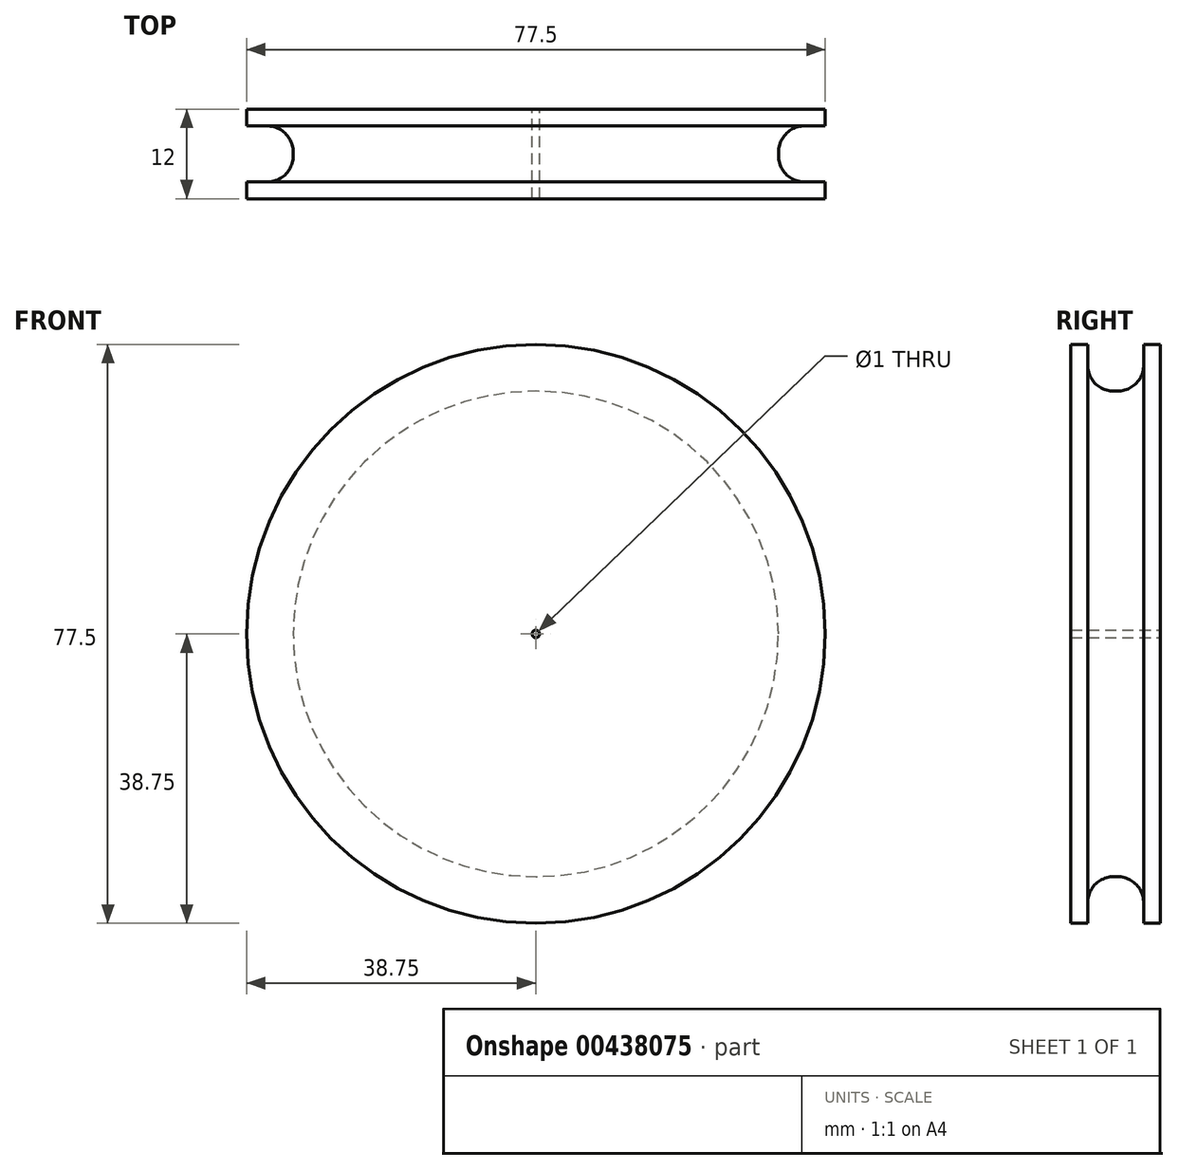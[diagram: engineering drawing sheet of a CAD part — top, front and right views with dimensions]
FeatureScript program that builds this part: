
annotation { "Feature Type Name" : "Feature", "Feature Type Description" : "" }
export const myFeature = defineFeature(function(context is Context, id is Id, definition is map)
    precondition{}
    {
        {
            var Q0;
            Q0=qCreatedBy(makeId("Front.planeOp"),FACE);
            var sketch = newSketch(context, id + "F0", { "sketchPlane" : qUnion([Q0])});
            skCircle(sketch, "E0", {"center": v(0, 0) * mm, "radius": 38.75 * mm});
            skSolve(sketch);
        }
        {
            var Q0;
            Q0=makeQuery(id+"F0.imprint","IMPRINT",FACE,{"disambiguationData":[TD([[makeQuery(id+"F0.imprint","IMPRINT",EDGE,{"derivedFrom":sQuery(id+"F0.wireOp",EDGE,"E0")}),1.0]])]});
            extrude(context, id + "F1", {"entities" : qUnion([Q0]), "endBound" : BoundingType.SYMMETRIC, "depth" : 12 * mm});
        }
        {
            var Q0;
            Q0=qCreatedBy(makeId("Right.planeOp"),FACE);
            var sketch = newSketch(context, id + "F2", { "sketchPlane" : qUnion([Q0])});
            skLineSegment(sketch, "E1.bottom", {"start": v(3.75, 40) * mm, "end": v(-3.75, 40) * mm});
            skLineSegment(sketch, "E1.top", {"start": v(0.25, 32.5) * mm, "end": v(-0.25, 32.5) * mm});
            skLineSegment(sketch, "E1.left", {"start": v(3.75, 40) * mm, "end": v(3.75, 36) * mm});
            skLineSegment(sketch, "E1.right", {"start": v(-3.75, 40) * mm, "end": v(-3.75, 36) * mm});
            skPoint(sketch, "E2.visualSharp", {"position": v(-3.75, 32.5) * mm});
            skArc(sketch, "E2.filletArc", {"start": v(-3.75, 36) * mm, "mid": v(-2.72, 33.53) * mm, "end": v(-0.25, 32.5) * mm});
            skPoint(sketch, "E3.visualSharp", {"position": v(3.75, 32.5) * mm});
            skArc(sketch, "E3.filletArc", {"start": v(0.25, 32.5) * mm, "mid": v(2.72, 33.53) * mm, "end": v(3.75, 36) * mm});
            skSolve(sketch);
        }
        {
            var Q0;
            Q0=qCreatedBy(makeId("Top.planeOp"),FACE);
            var sketch = newSketch(context, id + "F3", { "sketchPlane" : qUnion([Q0])});
            skLineSegment(sketch, "E4", {"start": v(0, 51.52) * mm, "end": v(0, -55.54) * mm});
            skSolve(sketch);
        }
        {
            var Q0;
            Q0 = qSketchRegion(id + "F2", true);
            var Q1;
            Q1=sQuery(id+"F3.wireOp",EDGE,"E4");
            var Q2;
            Q2=sQuery(id+"F3.wireOp",EDGE,"E4");
            revolve(context, id + "F4", {"operationType" : NewBodyOperationType.REMOVE, "entities" : qUnion([Q0]), "surfaceEntities" : qUnion([Q1]), "axis" : qUnion([Q2]), "revolveType" : RevolveType.FULL, "oppositeDirection" : true});
        }
        {
            var Q0;
            Q0=makeQuery(id+"F1.opExtrude","CAP_FACE",FACE,{"disambiguationData":[OSD([sQuery(id+"F0.wireOp",EDGE,"E0")])],"isStart":true});
            var sketch = newSketch(context, id + "F5", { "sketchPlane" : qUnion([Q0])});
            skCircle(sketch, "E5", {"center": v(0, 0) * mm, "radius": 0.5 * mm});
            skSolve(sketch);
        }
        {
            var Q0;
            Q0=makeQuery(id+"F5.imprint","IMPRINT",FACE,{"disambiguationData":[TD([[makeQuery(id+"F5.imprint","IMPRINT",EDGE,{"derivedFrom":sQuery(id+"F5.wireOp",EDGE,"E5")}),1.0]])]});
            extrude(context, id + "F6", {"entities" : qUnion([Q0]), "operationType" : NewBodyOperationType.REMOVE, "endBound" : BoundingType.THROUGH_ALL, "oppositeDirection" : true, "depth" : 25 * mm});
        }
    });
